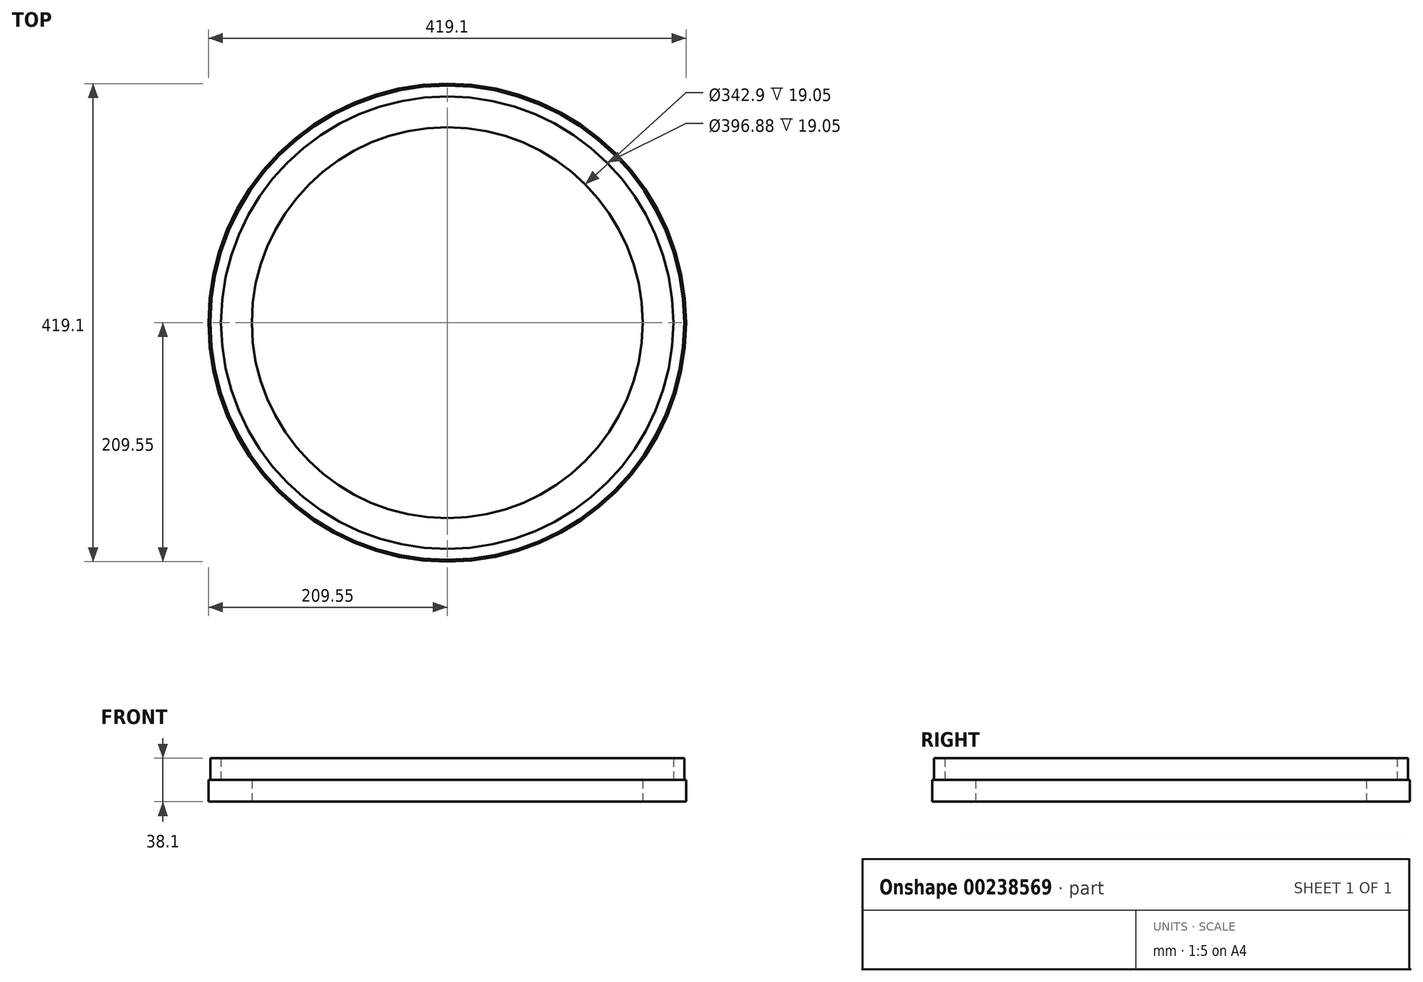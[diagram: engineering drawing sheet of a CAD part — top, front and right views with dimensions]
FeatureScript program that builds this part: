
annotation { "Feature Type Name" : "Feature", "Feature Type Description" : "" }
export const myFeature = defineFeature(function(context is Context, id is Id, definition is map)
    precondition{}
    {
        {
            var Q0;
            Q0=qCreatedBy(makeId("Top.planeOp"),FACE);
            var sketch = newSketch(context, id + "F0", { "sketchPlane" : qUnion([Q0])});
            skCircle(sketch, "E0", {"center": v(0, 0) * mm, "radius": 209.55 * mm});
            skSolve(sketch);
        }
        {
            var Q0;
            Q0=makeQuery(id+"F0.imprint","IMPRINT",FACE,{"disambiguationData":[TD([[makeQuery(id+"F0.imprint","IMPRINT",EDGE,{"derivedFrom":sQuery(id+"F0.wireOp",EDGE,"E0")}),1.0]])]});
            extrude(context, id + "F1", {"entities" : qUnion([Q0]), "depth" : 19.05 * mm});
        }
        {
            var Q0;
            Q0=makeQuery(id+"F1.opExtrude","CAP_FACE",FACE,{"disambiguationData":[OSD([sQuery(id+"F0.wireOp",EDGE,"E0")])],"isStart":true});
            var sketch = newSketch(context, id + "F2", { "sketchPlane" : qUnion([Q0])});
            skCircle(sketch, "E1", {"center": v(0, 0) * mm, "radius": 171.45 * mm});
            skSolve(sketch);
        }
        {
            var Q0;
            Q0=makeQuery(id+"F2.imprint","IMPRINT",FACE,{"disambiguationData":[TD([[makeQuery(id+"F2.imprint","IMPRINT",EDGE,{"derivedFrom":sQuery(id+"F2.wireOp",EDGE,"E1")}),1.0]])]});
            extrude(context, id + "F3", {"entities" : qUnion([Q0]), "operationType" : NewBodyOperationType.REMOVE, "oppositeDirection" : true, "depth" : 25.4 * mm});
        }
        {
            var Q0;
            Q0=makeQuery(id+"F1.opExtrude","CAP_FACE",FACE,{"disambiguationData":[OSD([sQuery(id+"F0.wireOp",EDGE,"E0")])],"isStart":false});
            var sketch = newSketch(context, id + "F4", { "sketchPlane" : qUnion([Q0])});
            skCircle(sketch, "E2", {"center": v(0, 0) * mm, "radius": 198.44 * mm});
            skCircle(sketch, "E3.0", {"center": v(0, 0) * mm, "radius": 207.96 * mm});
            skSolve(sketch);
        }
        {
            var Q0;
            Q0=makeQuery(id+"F4.imprint","IMPRINT",FACE,{"disambiguationData":[TD([[makeQuery(id+"F4.imprint","IMPRINT",EDGE,{"derivedFrom":sQuery(id+"F4.wireOp",EDGE,"E2")}),-1.0]])]});
            extrude(context, id + "F5", {"entities" : qUnion([Q0]), "operationType" : NewBodyOperationType.ADD, "depth" : 19.05 * mm});
        }
    });
